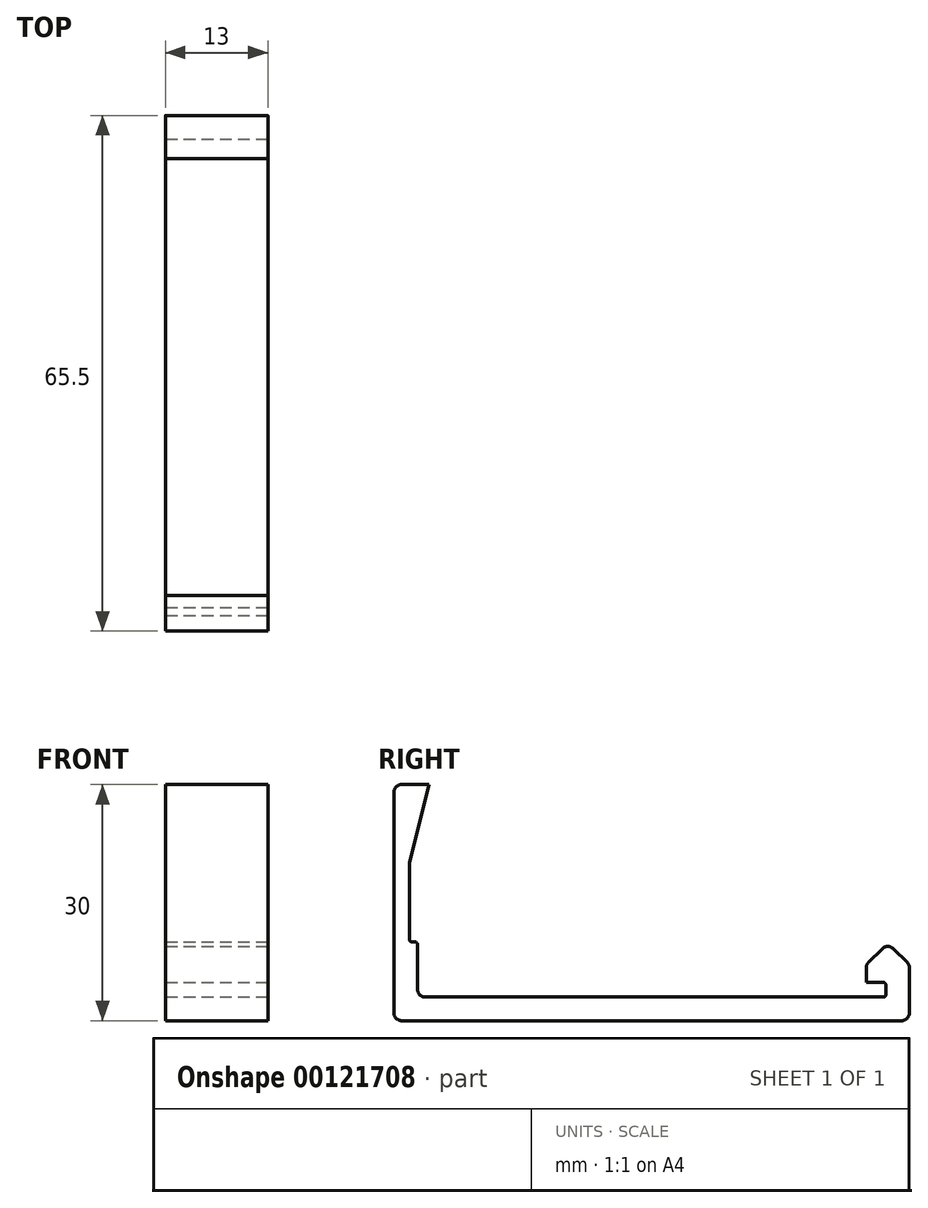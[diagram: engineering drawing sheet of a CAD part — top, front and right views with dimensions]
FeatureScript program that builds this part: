
annotation { "Feature Type Name" : "Feature", "Feature Type Description" : "" }
export const myFeature = defineFeature(function(context is Context, id is Id, definition is map)
    precondition{}
    {
        {
            assignVariable(context, id + "F0", {"name" : "width", "anyValue" : 13});
        }
        {
            var Q0;
            Q0=qCreatedBy(makeId("Right.planeOp"),FACE);
            var sketch = newSketch(context, id + "F1", { "sketchPlane" : qUnion([Q0])});
            skLineSegment(sketch, "E0", {"start": v(0, 0) * mm, "end": v(59.5, 0) * mm});
            skLineSegment(sketch, "E1", {"start": v(59.5, 0) * mm, "end": v(59.5, 1.85) * mm});
            skLineSegment(sketch, "E2", {"start": v(57, 1.85) * mm, "end": v(57, 4.1) * mm});
            skLineSegment(sketch, "E3", {"start": v(59.75, 6.85) * mm, "end": v(62.5, 4.1) * mm});
            skLineSegment(sketch, "E4", {"start": v(62.5, 4.1) * mm, "end": v(62.5, -3) * mm});
            skLineSegment(sketch, "E5", {"start": v(62.5, -3) * mm, "end": v(59.5, -3) * mm});
            skLineSegment(sketch, "E6", {"start": v(0, -3) * mm, "end": v(-3, -3) * mm});
            skLineSegment(sketch, "E7", {"start": v(-3, -3) * mm, "end": v(-3, 27) * mm});
            skLineSegment(sketch, "E8", {"start": v(-3, 27) * mm, "end": v(1.5, 27) * mm});
            skLineSegment(sketch, "E9", {"start": v(1.5, 27) * mm, "end": v(-1, 17) * mm});
            skLineSegment(sketch, "E10", {"start": v(59.5, -3) * mm, "end": v(0, -3) * mm});
            skLineSegment(sketch, "E11", {"start": v(57, 4.1) * mm, "end": v(59.75, 6.85) * mm});
            skLineSegment(sketch, "E12", {"start": v(59.5, 1.85) * mm, "end": v(57, 1.85) * mm});
            skLineSegment(sketch, "E13", {"start": v(-1, 7) * mm, "end": v(-1, 17) * mm});
            skLineSegment(sketch, "E14", {"start": v(0, 0) * mm, "end": v(0, 7) * mm});
            skLineSegment(sketch, "E15", {"start": v(0, 7) * mm, "end": v(-1, 7) * mm});
            skSolve(sketch);
        }
        {
            var Q0;
            {var subQ0=sQuery(id+"F1.wireOp",EDGE,"E0");Q0=makeQuery(id+"F1.imprint","IMPRINT",FACE,{"disambiguationData":[TD([[makeQuery(id+"F1.imprint","IMPRINT",EDGE,{"derivedFrom":subQ0}),-1.0]])]});}
            extrude(context, id + "F2", {"entities" : qUnion([Q0]), "endBound" : BoundingType.SYMMETRIC, "oppositeDirection" : true, "depth" : (getVariable(context, 'width')) * mm});
        }
        {
            var Q0;
            Q0=makeQuery(id+"F2.opExtrude","SWEPT_EDGE",EDGE,{"disambiguationData":[OSD([sQuery(id+"F1.wireOp",EDGE,"E4"),sQuery(id+"F1.wireOp",EDGE,"E5")])]});
            var Q1;
            Q1=makeQuery(id+"F2.opExtrude","SWEPT_EDGE",EDGE,{"disambiguationData":[OSD([sQuery(id+"F1.wireOp",EDGE,"E6"),sQuery(id+"F1.wireOp",EDGE,"E7")])]});
            var Q2;
            Q2=makeQuery(id+"F2.opExtrude","SWEPT_EDGE",EDGE,{"disambiguationData":[OSD([sQuery(id+"F1.wireOp",EDGE,"E7"),sQuery(id+"F1.wireOp",EDGE,"E8")])]});
            var Q3;
            Q3=makeQuery(id+"F2.opExtrude","SWEPT_EDGE",EDGE,{"disambiguationData":[OSD([sQuery(id+"F1.wireOp",EDGE,"E3"),sQuery(id+"F1.wireOp",EDGE,"E4")])]});
            var Q4;
            Q4=makeQuery(id+"F2.opExtrude","SWEPT_EDGE",EDGE,{"disambiguationData":[OSD([sQuery(id+"F1.wireOp",EDGE,"E3"),sQuery(id+"F1.wireOp",EDGE,"E11")])]});
            var Q5;
            Q5=makeQuery(id+"F2.opExtrude","SWEPT_EDGE",EDGE,{"disambiguationData":[OSD([sQuery(id+"F1.wireOp",EDGE,"E2"),sQuery(id+"F1.wireOp",EDGE,"E11")])]});
            var Q6;
            Q6=makeQuery(id+"F2.opExtrude","SWEPT_EDGE",EDGE,{"disambiguationData":[OSD([sQuery(id+"F1.wireOp",EDGE,"E0"),sQuery(id+"F1.wireOp",EDGE,"E14")])]});
            fillet(context, id + "F3", {"entities" : qUnion([Q0, Q1, Q2, Q3, Q4, Q5, Q6]), "radius" : 1 * mm, "tangentPropagation" : true, "allowEdgeOverflow" : false});
        }
        {
            var Q0;
            Q0=makeQuery(id+"F2.opExtrude","SWEPT_EDGE",EDGE,{"disambiguationData":[OSD([sQuery(id+"F1.wireOp",EDGE,"FelcoSfl-xoF4-9t4q-0NBy-nLNJwIf5QiqU"),sQuery(id+"F1.wireOp",EDGE,"E13")])]});
            var Q1;
            Q1=makeQuery(id+"F2.opExtrude","SWEPT_EDGE",EDGE,{"disambiguationData":[OSD([sQuery(id+"F1.wireOp",EDGE,"E9"),sQuery(id+"F1.wireOp",EDGE,"E13")])]});
            var Q2;
            Q2=makeQuery(id+"F2.opExtrude","SWEPT_EDGE",EDGE,{"disambiguationData":[OSD([sQuery(id+"F1.wireOp",EDGE,"E0"),sQuery(id+"F1.wireOp",EDGE,"E1")])]});
            var Q3;
            Q3=makeQuery(id+"F2.opExtrude","SWEPT_EDGE",EDGE,{"disambiguationData":[OSD([sQuery(id+"F1.wireOp",EDGE,"E1"),sQuery(id+"F1.wireOp",EDGE,"E12")])]});
            var Q4;
            Q4=makeQuery(id+"F2.opExtrude","SWEPT_EDGE",EDGE,{"disambiguationData":[OSD([sQuery(id+"F1.wireOp",EDGE,"E14"),sQuery(id+"F1.wireOp",EDGE,"E15")])]});
            fillet(context, id + "F4", {"entities" : qUnion([Q0, Q1, Q2, Q3, Q4]), "radius" : 0.3 * mm, "tangentPropagation" : true, "allowEdgeOverflow" : false});
        }
    });
